# Revit family: RN 23130 Valvola diritta sotto muro
name_source: partatom
category: Rohrzubehör
units: mm (PartAtom-declared; Revit-internal decimal feet)

## family parameters
Arbeitsebenenbasiert = Nein
Beim Laden mit Abzugskörper schneiden = Nein
Bemaßung runder Anschluss = Durchmesser verwenden
Gemeinsam genutzt = Nein
Immer vertikal = Ja
Teiletyp = Ventil - Zerlegung in

## types (3) — shared parameters
1.010.00.2 Blattnummer der Richtlinie = 17
1.010.00.3 Ausgabedatum (Monat) der Richtlinie = 201601
1.010.00.4 Herstellername = R. Nussbaum AG
1.010.00.5 Revisionsdatum der Datei = 20190528
1.010.00.6 Webadresse des Herstellers = http://www.nussbaum.ch
1.100.00.3 Sortiernummer für Anzeigereihenfolge = 1
1.100.00.4 Produktbezeichnung = Absperrarmaturen
1.960/3L.00.8 Link (URL) = https://www.nussbaum.ch
17.700.00.4 Armaturentyp = 1
17.700.00.7 Maximale Betriebstemperatur TB [°C] = 90
17.700.00.8 Maximaler Betriebsdruck (Arbeitsdruck) ps [1.0 · 105 Pa] = 16
Connector Visibility = Nein
EnclosingSpace Visibility = Nein
Hersteller = R. Nussbauzm AG
URL = https://www.nussbaum.ch

## per-type parameters (varying)
| type | 1.800.00.3 TGA-Nummer | 1.810.00.3 Hersteller-Bestellnummer | 1.810.00.4 DATANORM-Nummer | 1.810.00.5 StLB-Nummer | 1.810.00.6 GTIN-Nummer | 17.700.00.30 Produktbeschreibung | 17.700.00.5 Nennweite DN | 17.700.00.6 kvs-Wert [m3/h] | CONNECTOR0_DIAMETER_dZ_0r | CONNECTOR0_dZ_00 | CONNECTOR0_dZ_01 | CONNECTOR0_ref_dZ | CONNECTOR1_DIAMETER_dZ_0r | CONNECTOR1_dZ_00 | CONNECTOR1_dZ_01 | CONNECTOR1_ref_dZ | Modell | R. Nussbaum AG 23130.04 de Visibility | R. Nussbaum AG 23130.05 de Visibility | R. Nussbaum AG 23130.06 de Visibility | Typenkommentare |
| DN 15 | 00106600000000000000000000000200700000000000000001???00000 | 23130.04 | 23130.04 | 623.613 | 7612945736710 | 23130.04, Unterputz-Geradsitzventil, DN=15, Rp=½ | 15 | 4.93 | 15 mm | 38 mm | 25 mm  [stored 0.082021 ft] | 25 mm  [stored 0.082021 ft] | 15 mm | 25 mm  [stored 0.082021 ft] | 38 mm | 25 mm  [stored 0.082021 ft] | 23130.04 | Ja | Nein | Nein | Valvola diritta sotto muroDN 15 |
| DN 20 | 00106600000000000000000000000200700000000000000002???00000 | 23130.05 | 23130.05 | 623.614 | 7612945736727 | 23130.05, Unterputz-Geradsitzventil, DN=20, Rp=¾ | 20 | 6.07 | 20 mm | 38 mm | 23 mm  [stored 0.0754593 ft] | 23 mm  [stored 0.0754593 ft] | 20 mm | 23 mm  [stored 0.0754593 ft] | 38 mm | 23 mm  [stored 0.0754593 ft] | 23130.05 | Nein | Ja | Nein | Valvola diritta sotto muroDN 20 |
| DN 25 | 00106600000000000000000000000200700000000000000003???00000 | 23130.06 | 23130.06 | 623.615 | 7612945736734 | 23130.06, Unterputz-Geradsitzventil, DN=25, Rp=1 | 25 | 7.13 | 25 mm  [stored 0.082021 ft] | 48 mm | 31 mm | 31 mm | 25 mm  [stored 0.082021 ft] | 31 mm | 48 mm | 31 mm | 23130.06 | Nein | Nein | Ja | Valvola diritta sotto muroDN 25 |

note: [stored X ft] marks values corroborated as IEEE doubles in the binary element streams (Revit-internal decimal feet)

## geometry (parser evidence)
native form markers: Sweep x2
no freeform markers — native parametric forms only
